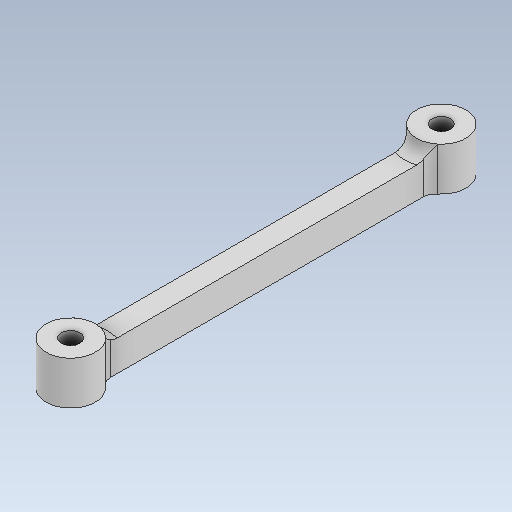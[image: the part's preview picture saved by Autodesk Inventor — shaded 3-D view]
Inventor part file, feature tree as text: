
AUTODESK INVENTOR PART (.ipt)
format: ipt  version: 2023 (Build 270158000, 158)  size: 140,288 bytes
history: native  units: mm
features: sketch x3, projected_geometry x3, extrude x2, hole x1, fillet x1
ambient origin geometry x8: Origin, YZ Plane, XZ Plane, XY Plane, X Axis, Y Axis, Z Axis, Center Point
bodies: Solid1 (feature_tree)
feature tree (10):
  extrude  "Extrusion1"  Depth=60.0mm
  extrude  "Extrusion2"  Depth=3.5mm
  hole  "Hole1"  [1 undecoded]
  fillet  "Fillet1"  Radius=8.0mm
  sketch  "Sketch1"  dims[d0=8.0mm d1=60.0mm]
  sketch  "Sketch2"  dims[d2=8.0mm d3=3.5mm]
  projected_geometry  "Projected Loop1"
  sketch  "Sketch3"  dims[d4=7.0mm d5=0.0mm d6=8.0mm d7=8.0mm d8=2.0mm d9=0.0mm d10=3.0mm d11=6.0mm d12=4.0mm d13=2.0mm d14=90.0deg d15=8.0mm d16=0.0mm d17=2.0mm]
  projected_geometry  "Projected Loop2"
  projected_geometry  "Projected Loop3"
note: 1 required parameter value undecoded (feature->parameter linkage not recoverable at this tier; creation-order binding heuristic only, values carry confidence <= 0.55)
